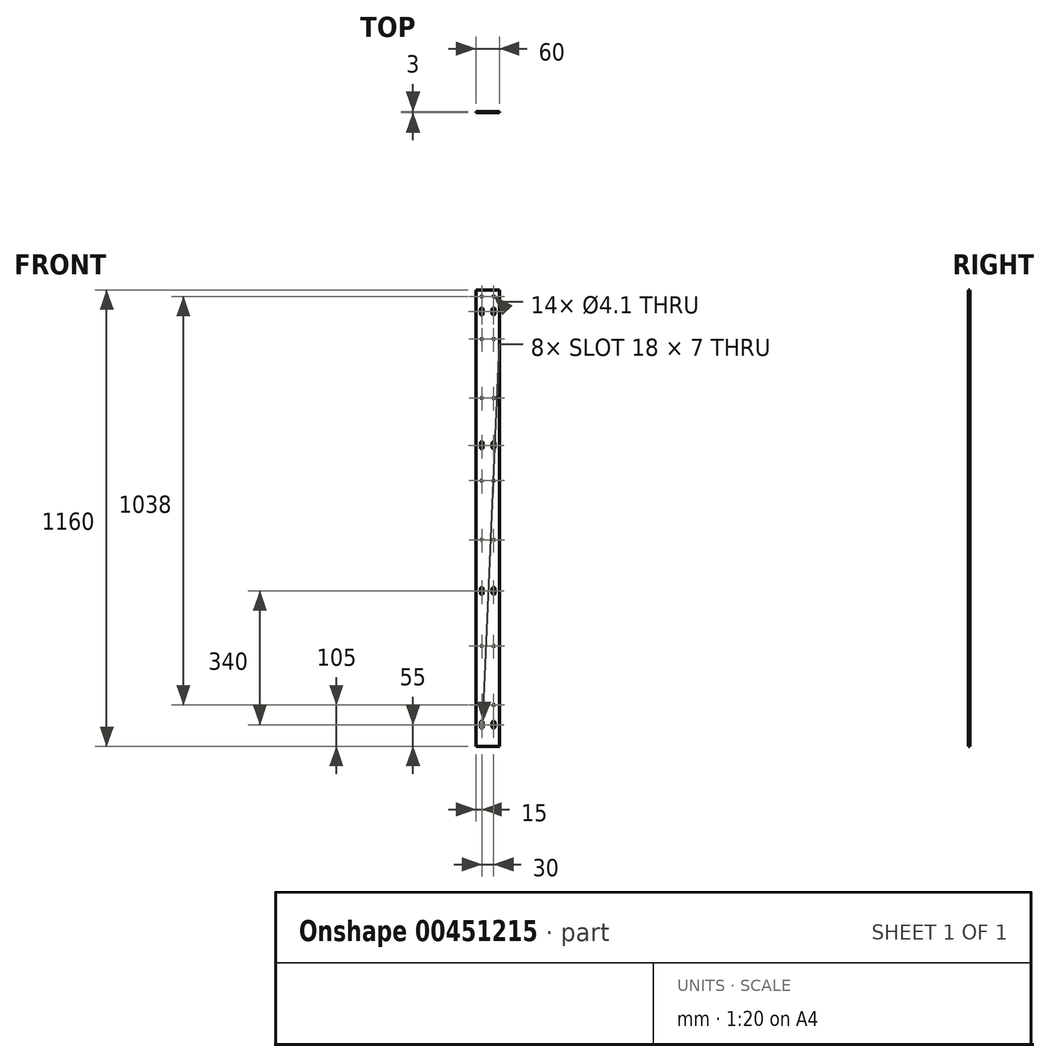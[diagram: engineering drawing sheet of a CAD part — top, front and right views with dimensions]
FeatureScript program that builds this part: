
annotation { "Feature Type Name" : "Feature", "Feature Type Description" : "" }
export const myFeature = defineFeature(function(context is Context, id is Id, definition is map)
    precondition{}
    {
        {
            var Q0;
            Q0=qCreatedBy(makeId("Front.planeOp"),FACE);
            var sketch = newSketch(context, id + "F0", { "sketchPlane" : qUnion([Q0])});
            skLineSegment(sketch, "E0.bottom", {"start": v(60, 0) * mm, "end": v(0, 0) * mm});
            skLineSegment(sketch, "E0.top", {"start": v(60, 1160) * mm, "end": v(0, 1160) * mm});
            skLineSegment(sketch, "E0.left", {"start": v(60, 0) * mm, "end": v(60, 1160) * mm});
            skLineSegment(sketch, "E0.right", {"start": v(0, 0) * mm, "end": v(0, 1160) * mm});
            skPoint(sketch, "E0.middle", {"position": v(30, 580) * mm});
            skLineSegment(sketch, "E1.bottom", {"start": v(18.5, 49.5) * mm, "end": v(11.5, 49.5) * mm, "construction": true});
            skLineSegment(sketch, "E1.top", {"start": v(18.5, 60.5) * mm, "end": v(11.5, 60.5) * mm, "construction": true});
            skLineSegment(sketch, "E1.left", {"start": v(18.5, 49.5) * mm, "end": v(18.5, 60.5) * mm});
            skLineSegment(sketch, "E1.right", {"start": v(11.5, 49.5) * mm, "end": v(11.5, 60.5) * mm});
            skPoint(sketch, "E1.middle", {"position": v(15, 55) * mm});
            skArc(sketch, "E2", {"start": v(18.5, 60.5) * mm, "mid": v(15, 64) * mm, "end": v(11.5, 60.5) * mm});
            skArc(sketch, "E3", {"start": v(11.5, 49.5) * mm, "mid": v(15, 46) * mm, "end": v(18.5, 49.5) * mm});
            skLineSegment(sketch, "E4.bottom", {"start": v(48.5, 49.5) * mm, "end": v(41.5, 49.5) * mm, "construction": true});
            skLineSegment(sketch, "E4.top", {"start": v(48.5, 60.5) * mm, "end": v(41.5, 60.5) * mm, "construction": true});
            skLineSegment(sketch, "E4.left", {"start": v(48.5, 49.5) * mm, "end": v(48.5, 60.5) * mm});
            skLineSegment(sketch, "E4.right", {"start": v(41.5, 49.5) * mm, "end": v(41.5, 60.5) * mm});
            skPoint(sketch, "E4.middle", {"position": v(45, 55) * mm});
            skArc(sketch, "E5", {"start": v(48.5, 60.5) * mm, "mid": v(45, 64) * mm, "end": v(41.5, 60.5) * mm});
            skArc(sketch, "E6", {"start": v(41.5, 49.5) * mm, "mid": v(45, 46) * mm, "end": v(48.5, 49.5) * mm});
            skLineSegment(sketch, "E7.bottom", {"start": v(18.5, 389.5) * mm, "end": v(11.5, 389.5) * mm, "construction": true});
            skLineSegment(sketch, "E7.top", {"start": v(18.5, 400.5) * mm, "end": v(11.5, 400.5) * mm, "construction": true});
            skLineSegment(sketch, "E7.left", {"start": v(18.5, 389.5) * mm, "end": v(18.5, 400.5) * mm});
            skLineSegment(sketch, "E7.right", {"start": v(11.5, 389.5) * mm, "end": v(11.5, 400.5) * mm});
            skPoint(sketch, "E7.middle", {"position": v(15, 395) * mm});
            skArc(sketch, "E8", {"start": v(18.5, 400.5) * mm, "mid": v(15, 404) * mm, "end": v(11.5, 400.5) * mm});
            skArc(sketch, "E9", {"start": v(11.5, 389.5) * mm, "mid": v(15, 386) * mm, "end": v(18.5, 389.5) * mm});
            skLineSegment(sketch, "E10.bottom", {"start": v(48.5, 389.5) * mm, "end": v(41.5, 389.5) * mm, "construction": true});
            skLineSegment(sketch, "E10.top", {"start": v(48.5, 400.5) * mm, "end": v(41.5, 400.5) * mm, "construction": true});
            skLineSegment(sketch, "E10.left", {"start": v(48.5, 389.5) * mm, "end": v(48.5, 400.5) * mm});
            skLineSegment(sketch, "E10.right", {"start": v(41.5, 389.5) * mm, "end": v(41.5, 400.5) * mm});
            skPoint(sketch, "E10.middle", {"position": v(45, 395) * mm});
            skArc(sketch, "E11", {"start": v(48.5, 400.5) * mm, "mid": v(45, 404) * mm, "end": v(41.5, 400.5) * mm});
            skArc(sketch, "E12", {"start": v(41.5, 389.5) * mm, "mid": v(45, 386) * mm, "end": v(48.5, 389.5) * mm});
            skLineSegment(sketch, "E13.bottom", {"start": v(18.5, 1099.5) * mm, "end": v(11.5, 1099.5) * mm, "construction": true});
            skLineSegment(sketch, "E13.top", {"start": v(18.5, 1110.5) * mm, "end": v(11.5, 1110.5) * mm, "construction": true});
            skLineSegment(sketch, "E13.left", {"start": v(18.5, 1099.5) * mm, "end": v(18.5, 1110.5) * mm});
            skLineSegment(sketch, "E13.right", {"start": v(11.5, 1099.5) * mm, "end": v(11.5, 1110.5) * mm});
            skPoint(sketch, "E13.middle", {"position": v(15, 1105) * mm});
            skArc(sketch, "E14", {"start": v(18.5, 1110.5) * mm, "mid": v(15, 1114) * mm, "end": v(11.5, 1110.5) * mm});
            skArc(sketch, "E15", {"start": v(11.5, 1099.5) * mm, "mid": v(15, 1096) * mm, "end": v(18.5, 1099.5) * mm});
            skLineSegment(sketch, "E16.bottom", {"start": v(48.5, 1099.5) * mm, "end": v(41.5, 1099.5) * mm, "construction": true});
            skLineSegment(sketch, "E16.top", {"start": v(48.5, 1110.5) * mm, "end": v(41.5, 1110.5) * mm, "construction": true});
            skLineSegment(sketch, "E16.left", {"start": v(48.5, 1099.5) * mm, "end": v(48.5, 1110.5) * mm});
            skLineSegment(sketch, "E16.right", {"start": v(41.5, 1099.5) * mm, "end": v(41.5, 1110.5) * mm});
            skPoint(sketch, "E16.middle", {"position": v(45, 1105) * mm});
            skArc(sketch, "E17", {"start": v(48.5, 1110.5) * mm, "mid": v(45, 1114) * mm, "end": v(41.5, 1110.5) * mm});
            skArc(sketch, "E18", {"start": v(41.5, 1099.5) * mm, "mid": v(45, 1096) * mm, "end": v(48.5, 1099.5) * mm});
            skLineSegment(sketch, "E19.bottom", {"start": v(18.5, 759.5) * mm, "end": v(11.5, 759.5) * mm, "construction": true});
            skLineSegment(sketch, "E19.top", {"start": v(18.5, 770.5) * mm, "end": v(11.5, 770.5) * mm, "construction": true});
            skLineSegment(sketch, "E19.left", {"start": v(18.5, 759.5) * mm, "end": v(18.5, 770.5) * mm});
            skLineSegment(sketch, "E19.right", {"start": v(11.5, 759.5) * mm, "end": v(11.5, 770.5) * mm});
            skPoint(sketch, "E19.middle", {"position": v(15, 765) * mm});
            skArc(sketch, "E20", {"start": v(18.5, 770.5) * mm, "mid": v(15, 774) * mm, "end": v(11.5, 770.5) * mm});
            skArc(sketch, "E21", {"start": v(11.5, 759.5) * mm, "mid": v(15, 756) * mm, "end": v(18.5, 759.5) * mm});
            skLineSegment(sketch, "E22.bottom", {"start": v(48.5, 759.5) * mm, "end": v(41.5, 759.5) * mm, "construction": true});
            skLineSegment(sketch, "E22.top", {"start": v(48.5, 770.5) * mm, "end": v(41.5, 770.5) * mm, "construction": true});
            skLineSegment(sketch, "E22.left", {"start": v(48.5, 759.5) * mm, "end": v(48.5, 770.5) * mm});
            skLineSegment(sketch, "E22.right", {"start": v(41.5, 759.5) * mm, "end": v(41.5, 770.5) * mm});
            skPoint(sketch, "E22.middle", {"position": v(45, 765) * mm});
            skArc(sketch, "E23", {"start": v(48.5, 770.5) * mm, "mid": v(45, 774) * mm, "end": v(41.5, 770.5) * mm});
            skArc(sketch, "E24", {"start": v(41.5, 759.5) * mm, "mid": v(45, 756) * mm, "end": v(48.5, 759.5) * mm});
            skSolve(sketch);
        }
        {
            var Q0;
            Q0 = qSketchRegion(id + "F0", true);
            extrude(context, id + "F1", {"entities" : qUnion([Q0]), "depth" : 3 * mm, "offsetDistance" : 25 * mm});
        }
        {
            var Q0;
            Q0=makeQuery(id+"F1.opExtrude","CAP_FACE",FACE,{"disambiguationData":[OSD([sQuery(id+"F0.wireOp",EDGE,"E0.bottom"),sQuery(id+"F0.wireOp",EDGE,"E0.top"),sQuery(id+"F0.wireOp",EDGE,"E0.left"),sQuery(id+"F0.wireOp",EDGE,"E0.right"),sQuery(id+"F0.wireOp",EDGE,"E1.left"),sQuery(id+"F0.wireOp",EDGE,"E1.right"),sQuery(id+"F0.wireOp",EDGE,"E2"),sQuery(id+"F0.wireOp",EDGE,"E3"),sQuery(id+"F0.wireOp",EDGE,"E4.left"),sQuery(id+"F0.wireOp",EDGE,"E4.right"),sQuery(id+"F0.wireOp",EDGE,"E5"),sQuery(id+"F0.wireOp",EDGE,"E6"),sQuery(id+"F0.wireOp",EDGE,"E7.left"),sQuery(id+"F0.wireOp",EDGE,"E7.right"),sQuery(id+"F0.wireOp",EDGE,"E8"),sQuery(id+"F0.wireOp",EDGE,"E9"),sQuery(id+"F0.wireOp",EDGE,"E10.left"),sQuery(id+"F0.wireOp",EDGE,"E10.right"),sQuery(id+"F0.wireOp",EDGE,"E11"),sQuery(id+"F0.wireOp",EDGE,"E12"),sQuery(id+"F0.wireOp",EDGE,"E13.left"),sQuery(id+"F0.wireOp",EDGE,"E13.right"),sQuery(id+"F0.wireOp",EDGE,"E14"),sQuery(id+"F0.wireOp",EDGE,"E15"),sQuery(id+"F0.wireOp",EDGE,"E16.left"),sQuery(id+"F0.wireOp",EDGE,"E16.right"),sQuery(id+"F0.wireOp",EDGE,"E17"),sQuery(id+"F0.wireOp",EDGE,"E18")])],"isStart":false});
            var sketch = newSketch(context, id + "F2", { "sketchPlane" : qUnion([Q0])});
            skCircle(sketch, "E25", {"center": v(15, 105) * mm, "radius": 2.05 * mm});
            skCircle(sketch, "E26", {"center": v(45, 105) * mm, "radius": 2.05 * mm});
            skCircle(sketch, "E27", {"center": v(15, 255) * mm, "radius": 2.05 * mm});
            skCircle(sketch, "E28", {"center": v(45, 255) * mm, "radius": 2.05 * mm});
            skCircle(sketch, "E29", {"center": v(15, 525) * mm, "radius": 2.05 * mm});
            skCircle(sketch, "E30", {"center": v(45, 525) * mm, "radius": 2.05 * mm});
            skCircle(sketch, "E31", {"center": v(15, 675) * mm, "radius": 2.05 * mm});
            skCircle(sketch, "E32", {"center": v(45, 675) * mm, "radius": 2.05 * mm});
            skCircle(sketch, "E33", {"center": v(15, 885) * mm, "radius": 2.05 * mm});
            skCircle(sketch, "E34", {"center": v(45, 885) * mm, "radius": 2.05 * mm});
            skCircle(sketch, "E35", {"center": v(15, 1035) * mm, "radius": 2.05 * mm});
            skCircle(sketch, "E36", {"center": v(45, 1035) * mm, "radius": 2.05 * mm});
            skCircle(sketch, "E37", {"center": v(15, 1143) * mm, "radius": 2.05 * mm});
            skCircle(sketch, "E38", {"center": v(45, 1143) * mm, "radius": 2.05 * mm});
            skSolve(sketch);
        }
        {
            var Q0;
            Q0 = qSketchRegion(id + "F2", true);
            extrude(context, id + "F3", {"entities" : qUnion([Q0]), "operationType" : NewBodyOperationType.REMOVE, "oppositeDirection" : true, "depth" : 25 * mm, "offsetDistance" : 25 * mm});
        }
    });
